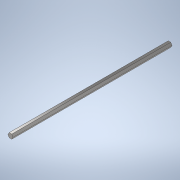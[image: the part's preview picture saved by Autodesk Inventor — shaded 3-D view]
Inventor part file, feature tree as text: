
AUTODESK INVENTOR PART (.ipt)
format: ipt  version: 2020 (Build 240168000, 168)  size: 103,936 bytes
history: native  units: in
note: dims shown in document units (in); Inventor stores cm internally (conversion verified against a paired STEP export)
features: extrude x1, sketch x1
ambient origin geometry x8: Origin, YZ Plane, XZ Plane, XY Plane, X Axis, Y Axis, Z Axis, Center Point
bodies: Solid1 (feature_tree)
feature tree (2):
  extrude  "Extrusion1"  Depth=18.0in TaperAngle=0.0deg
  sketch  "Sketch1"  dims[d0=0.5in d1=18.0in d2=0.0in]
